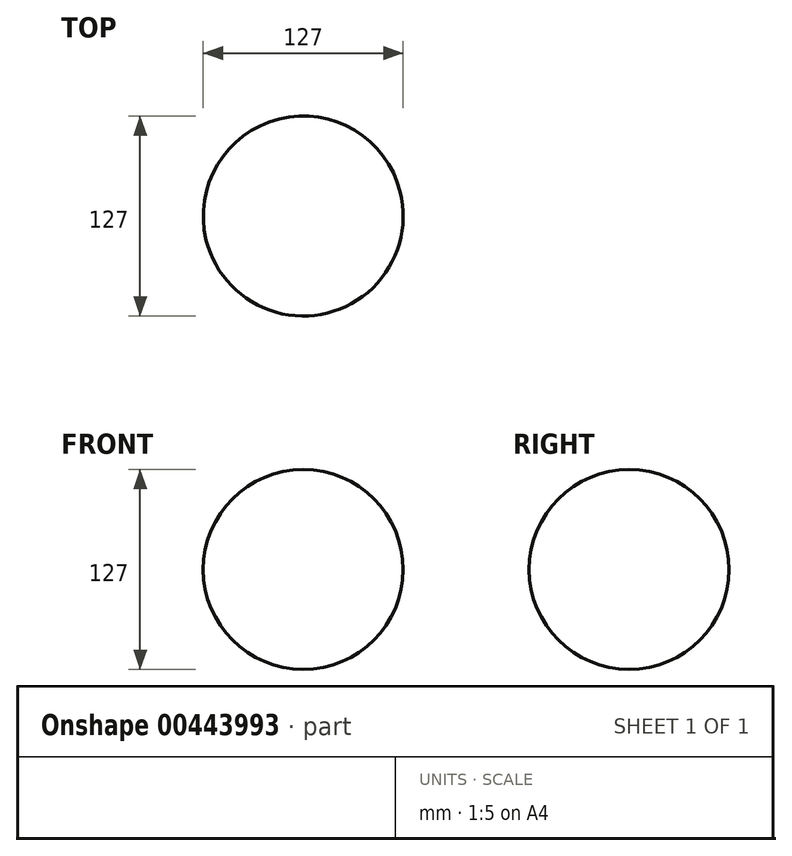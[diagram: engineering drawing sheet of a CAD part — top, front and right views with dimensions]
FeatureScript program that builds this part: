
annotation { "Feature Type Name" : "Feature", "Feature Type Description" : "" }
export const myFeature = defineFeature(function(context is Context, id is Id, definition is map)
    precondition{}
    {
        {
            var Q0;
            Q0=qCreatedBy(makeId("Top.planeOp"),FACE);
            var sketch = newSketch(context, id + "F0", { "sketchPlane" : qUnion([Q0])});
            skCircle(sketch, "E0", {"center": v(0, 0) * mm, "radius": 63.5 * mm});
            skLineSegment(sketch, "E1", {"start": v(-61.6, -15.42) * mm, "end": v(0, 0) * mm});
            skLineSegment(sketch, "E2", {"start": v(0, 0) * mm, "end": v(61.6, 15.42) * mm});
            skSolve(sketch);
        }
        {
            var Q0;
            {var subQ0=sQuery(id+"F0.wireOp",EDGE,"E1");Q0=makeQuery(id+"F0.imprint","IMPRINT",FACE,{"disambiguationData":[TD([[makeQuery(id+"F0.imprint","IMPRINT",EDGE,{"derivedFrom":subQ0}),1.0]])]});}
            var Q1;
            Q1=sQuery(id+"F0.wireOp",EDGE,"E1");
            revolve(context, id + "F1", {"entities" : qUnion([Q0]), "axis" : qUnion([Q1]), "revolveType" : RevolveType.FULL});
        }
    });
